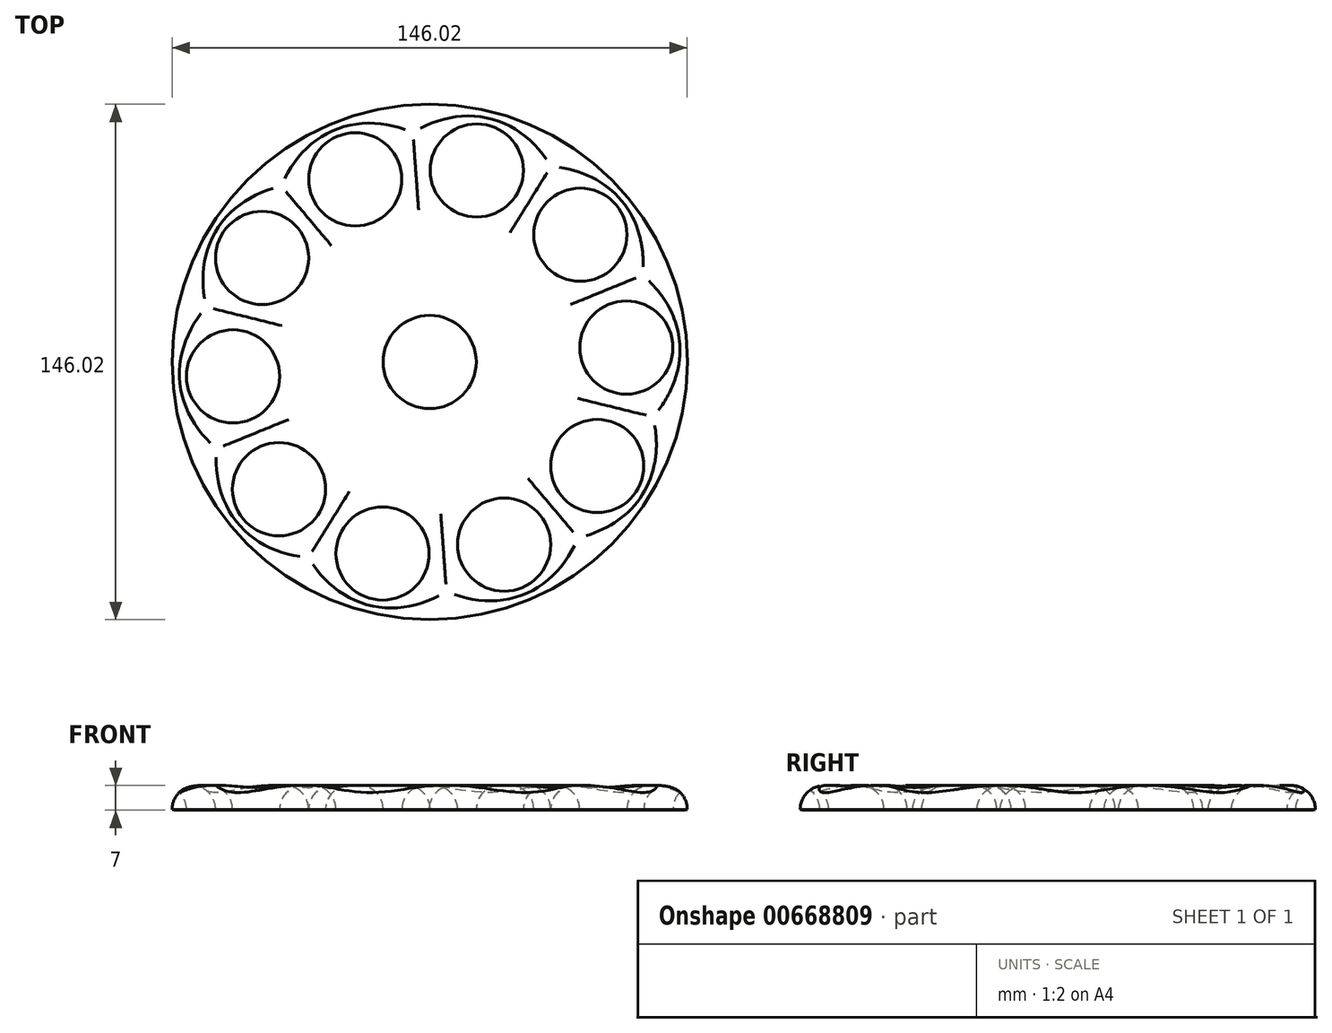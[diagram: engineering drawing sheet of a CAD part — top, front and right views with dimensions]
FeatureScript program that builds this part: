
annotation { "Feature Type Name" : "Feature", "Feature Type Description" : "" }
export const myFeature = defineFeature(function(context is Context, id is Id, definition is map)
    precondition{}
    {
        {
            var Q0;
            Q0=qCreatedBy(makeId("Top.planeOp"),FACE);
            var sketch = newSketch(context, id + "F0", { "sketchPlane" : qUnion([Q0])});
            skCircle(sketch, "E0", {"center": v(0, 0) * mm, "radius": 11.2 * mm});
            skCircle(sketch, "E1", {"center": v(0, 0) * mm, "radius": 13.2 * mm});
            skCircle(sketch, "E2", {"center": v(0, 0) * mm, "radius": 73.01 * mm});
            skCircle(sketch, "E3", {"center": v(-47.49, 29.47) * mm, "radius": 11.2 * mm});
            skCircle(sketch, "E4", {"center": v(-47.49, 29.47) * mm, "radius": 13.2 * mm});
            skCircle(sketch, "E5.1.0", {"center": v(-55.74, -4.07) * mm, "radius": 13.2 * mm});
            skCircle(sketch, "E5.1.1", {"center": v(-55.74, -4.07) * mm, "radius": 11.2 * mm});
            skCircle(sketch, "E5.2.0", {"center": v(-42.7, -36.06) * mm, "radius": 13.2 * mm});
            skCircle(sketch, "E5.2.1", {"center": v(-42.7, -36.06) * mm, "radius": 11.2 * mm});
            skCircle(sketch, "E5.3.0", {"center": v(-13.35, -54.27) * mm, "radius": 13.2 * mm});
            skCircle(sketch, "E5.3.1", {"center": v(-13.35, -54.27) * mm, "radius": 11.2 * mm});
            skCircle(sketch, "E5.4.0", {"center": v(21.1, -51.75) * mm, "radius": 13.2 * mm});
            skCircle(sketch, "E5.4.1", {"center": v(21.1, -51.75) * mm, "radius": 11.2 * mm});
            skCircle(sketch, "E5.5.0", {"center": v(47.49, -29.47) * mm, "radius": 13.2 * mm});
            skCircle(sketch, "E5.5.1", {"center": v(47.49, -29.47) * mm, "radius": 11.2 * mm});
            skCircle(sketch, "E5.6.0", {"center": v(55.74, 4.07) * mm, "radius": 13.2 * mm});
            skCircle(sketch, "E5.6.1", {"center": v(55.74, 4.07) * mm, "radius": 11.2 * mm});
            skCircle(sketch, "E5.7.0", {"center": v(42.7, 36.06) * mm, "radius": 13.2 * mm});
            skCircle(sketch, "E5.7.1", {"center": v(42.7, 36.06) * mm, "radius": 11.2 * mm});
            skCircle(sketch, "E5.8.0", {"center": v(13.35, 54.27) * mm, "radius": 13.2 * mm});
            skCircle(sketch, "E5.8.1", {"center": v(13.35, 54.27) * mm, "radius": 11.2 * mm});
            skCircle(sketch, "E5.9.0", {"center": v(-21.1, 51.75) * mm, "radius": 13.2 * mm});
            skCircle(sketch, "E5.9.1", {"center": v(-21.1, 51.75) * mm, "radius": 11.2 * mm});
            skSolve(sketch);
        }
        {
            var Q0;
            Q0=makeQuery(id+"F0.imprint","IMPRINT",FACE,{"disambiguationData":[TD([[makeQuery(id+"F0.imprint","IMPRINT",EDGE,{"derivedFrom":sQuery(id+"F0.wireOp",EDGE,"E1")}),-1.0]])]});
            extrude(context, id + "F1", {"entities" : qUnion([Q0]), "depth" : 7 * mm, "offsetDistance" : 25 * mm});
        }
        {
            var Q0;
            Q0=makeQuery(id+"F1.opExtrude","CAP_FACE",FACE,{"disambiguationData":[OSD([sQuery(id+"F0.wireOp",EDGE,"E1"),sQuery(id+"F0.wireOp",EDGE,"E2"),sQuery(id+"F0.wireOp",EDGE,"E4"),sQuery(id+"F0.wireOp",EDGE,"E5.1.0"),sQuery(id+"F0.wireOp",EDGE,"E5.2.0"),sQuery(id+"F0.wireOp",EDGE,"E5.3.0"),sQuery(id+"F0.wireOp",EDGE,"E5.4.0"),sQuery(id+"F0.wireOp",EDGE,"E5.5.0"),sQuery(id+"F0.wireOp",EDGE,"E5.6.0"),sQuery(id+"F0.wireOp",EDGE,"E5.7.0"),sQuery(id+"F0.wireOp",EDGE,"E5.8.0"),sQuery(id+"F0.wireOp",EDGE,"E5.9.0")])],"isStart":false});
            fillet(context, id + "F2", {"entities" : qUnion([Q0]), "tangentPropagation" : true, "radius" : 6.76 * mm, "defaultsChanged" : true, "vertexSettings" : [], "allowEdgeOverflow" : false});
        }
        {
            var Q0;
            Q0=makeQuery(id+"F1.opExtrude","CAP_FACE",FACE,{"disambiguationData":[OSD([sQuery(id+"F0.wireOp",EDGE,"E1"),sQuery(id+"F0.wireOp",EDGE,"E2"),sQuery(id+"F0.wireOp",EDGE,"E4"),sQuery(id+"F0.wireOp",EDGE,"E5.1.0"),sQuery(id+"F0.wireOp",EDGE,"E5.2.0"),sQuery(id+"F0.wireOp",EDGE,"E5.3.0"),sQuery(id+"F0.wireOp",EDGE,"E5.4.0"),sQuery(id+"F0.wireOp",EDGE,"E5.5.0"),sQuery(id+"F0.wireOp",EDGE,"E5.6.0"),sQuery(id+"F0.wireOp",EDGE,"E5.7.0"),sQuery(id+"F0.wireOp",EDGE,"E5.8.0"),sQuery(id+"F0.wireOp",EDGE,"E5.9.0")])],"isStart":true});
            fillet(context, id + "F3", {"entities" : qUnion([Q0]), "tangentPropagation" : true, "radius" : 5 * mm, "defaultsChanged" : false, "vertexSettings" : [], "allowEdgeOverflow" : false});
        }
    });
